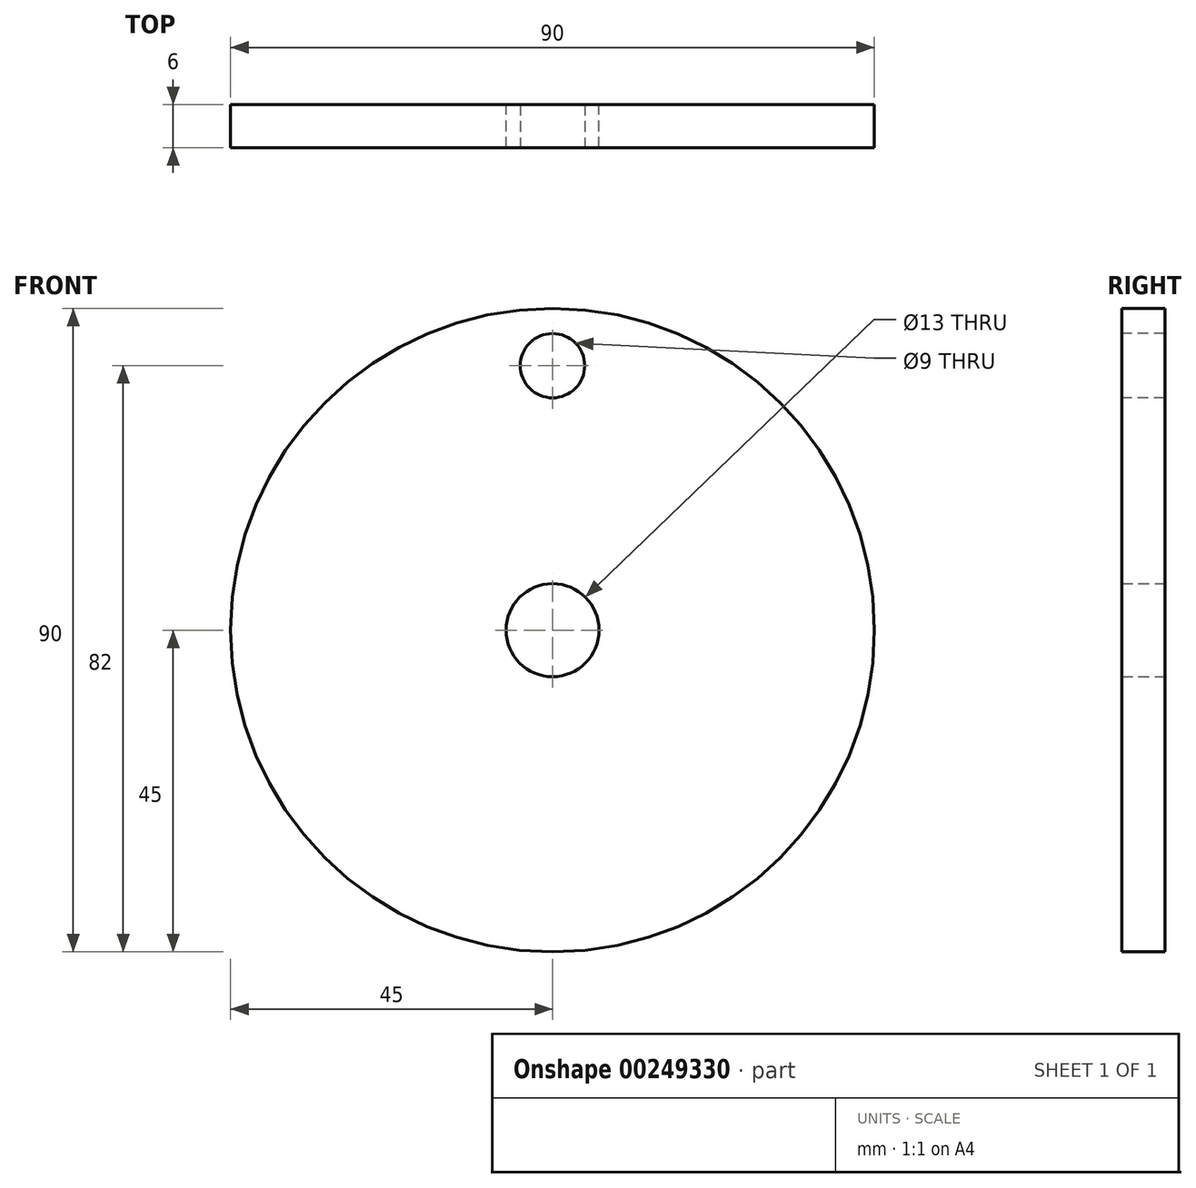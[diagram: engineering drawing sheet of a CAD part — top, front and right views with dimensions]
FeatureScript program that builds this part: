
annotation { "Feature Type Name" : "Feature", "Feature Type Description" : "" }
export const myFeature = defineFeature(function(context is Context, id is Id, definition is map)
    precondition{}
    {
        {
            var Q0;
            Q0=qCreatedBy(makeId("Front.planeOp"),FACE);
            var sketch = newSketch(context, id + "F0", { "sketchPlane" : qUnion([Q0])});
            skCircle(sketch, "E0", {"center": v(0, 0) * mm, "radius": 45 * mm});
            skCircle(sketch, "E1", {"center": v(0, 0) * mm, "radius": 6.5 * mm});
            skSolve(sketch);
        }
        {
            var Q0;
            Q0=makeQuery(id+"F0.imprint","IMPRINT",FACE,{"disambiguationData":[TD([[makeQuery(id+"F0.imprint","IMPRINT",EDGE,{"derivedFrom":sQuery(id+"F0.wireOp",EDGE,"E0")}),1.0]])]});
            extrude(context, id + "F1", {"entities" : qUnion([Q0]), "depth" : 6 * mm, "symmetric" : true});
        }
        {
            var Q0;
            Q0=makeQuery(id+"F1.opExtrude","CAP_FACE",FACE,{"disambiguationData":[OSD([sQuery(id+"F0.wireOp",EDGE,"E0"),sQuery(id+"F0.wireOp",EDGE,"E1")])],"isStart":false});
            var sketch = newSketch(context, id + "F2", { "sketchPlane" : qUnion([Q0])});
            skCircle(sketch, "E2", {"center": v(0, 37) * mm, "radius": 4.5 * mm});
            skSolve(sketch);
        }
        {
            var Q0;
            Q0=makeQuery(id+"F2.imprint","IMPRINT",FACE,{"disambiguationData":[TD([[makeQuery(id+"F2.imprint","IMPRINT",EDGE,{"derivedFrom":sQuery(id+"F2.wireOp",EDGE,"E2")}),1.0]])]});
            extrude(context, id + "F3", {"entities" : qUnion([Q0]), "operationType" : NewBodyOperationType.REMOVE, "oppositeDirection" : true, "depth" : 25 * mm});
        }
    });
